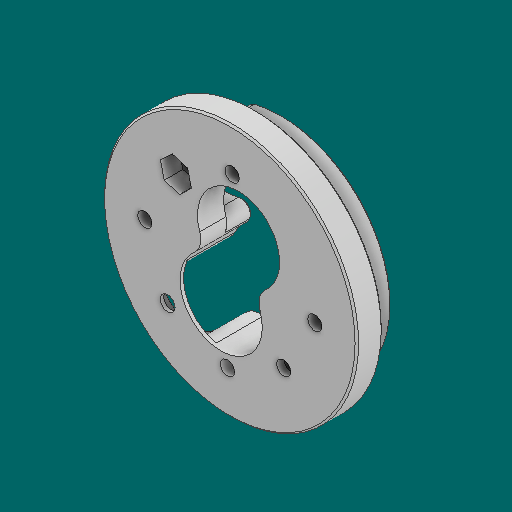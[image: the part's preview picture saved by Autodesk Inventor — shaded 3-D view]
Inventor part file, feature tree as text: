
AUTODESK INVENTOR PART (.ipt)
format: ipt  version: 2023.1 (Build 271208000, 208)  size: 294,400 bytes
history: native  units: in
note: dims shown in document units (in); Inventor stores cm internally (conversion verified against a paired STEP export)
features: sketch x6, other x3
ambient origin geometry x8: Origin, YZ Plane, XZ Plane, XY Plane, X Axis, Y Axis, Z Axis, Center Point
bodies: Solid1 (feature_tree)
feature tree (9):
  other  "UpperRingSeat_MIR.ipt"
  other  "Solid1::UpperRingSeat_MIR.ipt"
  other  "TaggingFeature1"
  sketch  "Sketch1"  dims[d0=0.3937in]
  sketch  "Sketch2"
  sketch  "Sketch3"
  sketch  "Sketch4"
  sketch  "Sketch5"
  sketch  "Sketch6"
